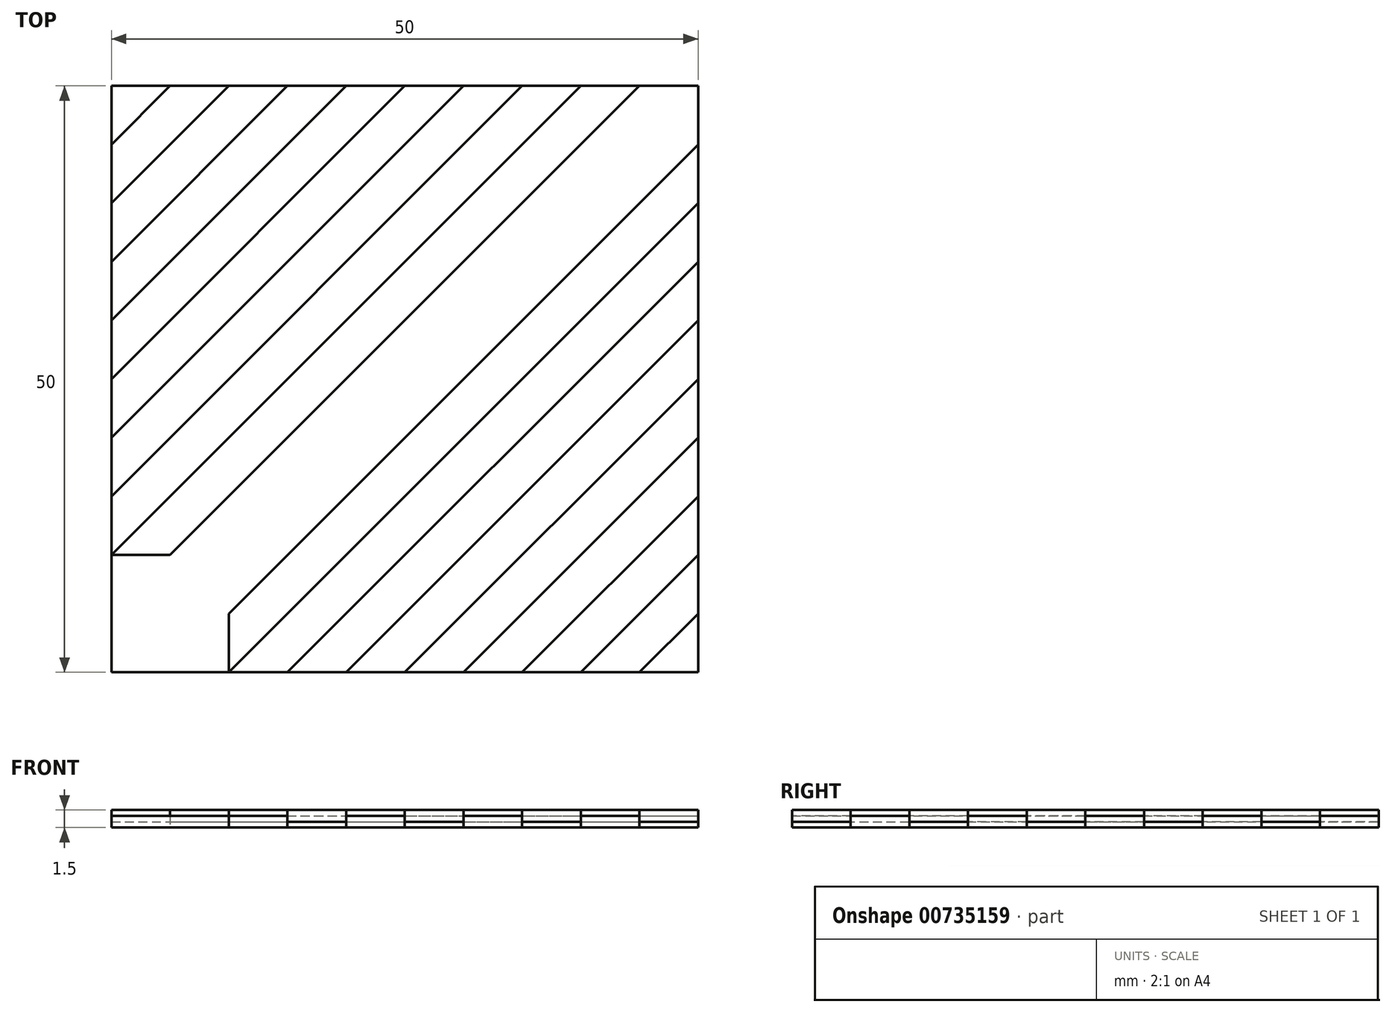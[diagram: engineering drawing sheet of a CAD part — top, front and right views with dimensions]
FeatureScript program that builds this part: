
annotation { "Feature Type Name" : "Feature", "Feature Type Description" : "" }
export const myFeature = defineFeature(function(context is Context, id is Id, definition is map)
    precondition{}
    {
        {
            var Q0;
            Q0=qCreatedBy(makeId("Top.planeOp"),FACE);
            var sketch = newSketch(context, id + "F0", { "sketchPlane" : qUnion([Q0])});
            skLineSegment(sketch, "E0.bottom", {"start": v(0, 50) * mm, "end": v(50, 50) * mm});
            skLineSegment(sketch, "E0.top", {"start": v(0, -50) * mm, "end": v(50, -50) * mm});
            skLineSegment(sketch, "E0.left", {"start": v(0, 50) * mm, "end": v(0, -50) * mm});
            skLineSegment(sketch, "E0.right", {"start": v(50, 50) * mm, "end": v(50, -50) * mm});
            skLineSegment(sketch, "E1", {"start": v(0, 10) * mm, "end": v(10, 10) * mm});
            skLineSegment(sketch, "E2", {"start": v(10, 10) * mm, "end": v(10, -10) * mm});
            skLineSegment(sketch, "E3", {"start": v(10, -10) * mm, "end": v(0, -10) * mm});
            skLineSegment(sketch, "E4", {"start": v(5, 10) * mm, "end": v(45, 50) * mm});
            skLineSegment(sketch, "E5", {"start": v(10, 10) * mm, "end": v(50, 50) * mm});
            skLineSegment(sketch, "E6", {"start": v(0, 10) * mm, "end": v(40, 50) * mm});
            skLineSegment(sketch, "E7", {"start": v(0, 15) * mm, "end": v(35, 50) * mm});
            skLineSegment(sketch, "E8", {"start": v(0, 20) * mm, "end": v(30, 50) * mm});
            skLineSegment(sketch, "E9", {"start": v(0, 25) * mm, "end": v(25, 50) * mm});
            skLineSegment(sketch, "E10", {"start": v(0, 30) * mm, "end": v(20, 50) * mm});
            skLineSegment(sketch, "E11", {"start": v(0, 35) * mm, "end": v(15, 50) * mm});
            skLineSegment(sketch, "E12", {"start": v(0, 40) * mm, "end": v(10, 50) * mm});
            skLineSegment(sketch, "E13", {"start": v(0, 45) * mm, "end": v(5, 50) * mm});
            skLineSegment(sketch, "E14", {"start": v(10, 5) * mm, "end": v(50, 45) * mm});
            skLineSegment(sketch, "E15", {"start": v(10, 0) * mm, "end": v(50, 40) * mm});
            skLineSegment(sketch, "E16", {"start": v(15, 0) * mm, "end": v(50, 35) * mm});
            skLineSegment(sketch, "E17", {"start": v(20, 0) * mm, "end": v(50, 30) * mm});
            skLineSegment(sketch, "E18", {"start": v(25, 0) * mm, "end": v(50, 25) * mm});
            skLineSegment(sketch, "E19", {"start": v(30, 0) * mm, "end": v(50, 20) * mm});
            skLineSegment(sketch, "E20", {"start": v(35, 0) * mm, "end": v(50, 15) * mm});
            skLineSegment(sketch, "E21", {"start": v(40, 0) * mm, "end": v(50, 10) * mm});
            skLineSegment(sketch, "E22", {"start": v(45, 0) * mm, "end": v(50, 5) * mm});
            skLineSegment(sketch, "E23", {"start": v(0, 0) * mm, "end": v(10, 0) * mm});
            skLineSegment(sketch, "E24", {"start": v(10, 0) * mm, "end": v(50, 0) * mm});
            skSolve(sketch);
        }
        {
            var Q0;
            {var subQ7=sQuery(id+"F0.wireOp",EDGE,"E23");Q0=makeQuery(id+"F0.imprint","IMPRINT",FACE,{"disambiguationData":[TD([[makeQuery(id+"F0.imprint","IMPRINT",EDGE,{"derivedFrom":subQ7}),1.0]])]});}
            var Q1;
            {var subQ2=sQuery(id+"F0.wireOp",EDGE,"E4");Q1=makeQuery(id+"F0.imprint","IMPRINT",FACE,{"disambiguationData":[TD([[makeQuery(id+"F0.imprint","IMPRINT",EDGE,{"derivedFrom":subQ2}),-1.0]])]});}
            var Q2;
            {var subQ0=sQuery(id+"F0.wireOp",EDGE,"E5");Q2=makeQuery(id+"F0.imprint","IMPRINT",FACE,{"disambiguationData":[TD([[makeQuery(id+"F0.imprint","IMPRINT",EDGE,{"derivedFrom":subQ0}),-1.0]])]});}
            var Q3;
            {var subQ0=sQuery(id+"F0.wireOp",EDGE,"E15");Q3=makeQuery(id+"F0.imprint","IMPRINT",FACE,{"disambiguationData":[TD([[makeQuery(id+"F0.imprint","IMPRINT",EDGE,{"derivedFrom":subQ0}),-1.0]])]});}
            var Q4;
            {var subQ0=sQuery(id+"F0.wireOp",EDGE,"E6");Q4=makeQuery(id+"F0.imprint","IMPRINT",FACE,{"disambiguationData":[TD([[makeQuery(id+"F0.imprint","IMPRINT",EDGE,{"derivedFrom":subQ0}),1.0]])]});}
            var Q5;
            {var subQ0=sQuery(id+"F0.wireOp",EDGE,"E17");Q5=makeQuery(id+"F0.imprint","IMPRINT",FACE,{"disambiguationData":[TD([[makeQuery(id+"F0.imprint","IMPRINT",EDGE,{"derivedFrom":subQ0}),-1.0]])]});}
            var Q6;
            {var subQ0=sQuery(id+"F0.wireOp",EDGE,"E8");Q6=makeQuery(id+"F0.imprint","IMPRINT",FACE,{"disambiguationData":[TD([[makeQuery(id+"F0.imprint","IMPRINT",EDGE,{"derivedFrom":subQ0}),1.0]])]});}
            var Q7;
            {var subQ0=sQuery(id+"F0.wireOp",EDGE,"E19");Q7=makeQuery(id+"F0.imprint","IMPRINT",FACE,{"disambiguationData":[TD([[makeQuery(id+"F0.imprint","IMPRINT",EDGE,{"derivedFrom":subQ0}),-1.0]])]});}
            var Q8;
            {var subQ0=sQuery(id+"F0.wireOp",EDGE,"E10");Q8=makeQuery(id+"F0.imprint","IMPRINT",FACE,{"disambiguationData":[TD([[makeQuery(id+"F0.imprint","IMPRINT",EDGE,{"derivedFrom":subQ0}),1.0]])]});}
            var Q9;
            {var subQ0=sQuery(id+"F0.wireOp",EDGE,"E21");Q9=makeQuery(id+"F0.imprint","IMPRINT",FACE,{"disambiguationData":[TD([[makeQuery(id+"F0.imprint","IMPRINT",EDGE,{"derivedFrom":subQ0}),-1.0]])]});}
            var Q10;
            {var subQ0=sQuery(id+"F0.wireOp",EDGE,"E12");Q10=makeQuery(id+"F0.imprint","IMPRINT",FACE,{"disambiguationData":[TD([[makeQuery(id+"F0.imprint","IMPRINT",EDGE,{"derivedFrom":subQ0}),1.0]])]});}
            extrude(context, id + "F1", {"entities" : qUnion([Q0, Q1, Q2, Q3, Q4, Q5, Q6, Q7, Q8, Q9, Q10]), "endBound" : BoundingType.SYMMETRIC, "depth" : 1 * mm, "offsetDistance" : 25 * mm});
        }
        {
            var Q0;
            {var subQ3=sQuery(id+"F0.wireOp",EDGE,"E13");Q0=makeQuery(id+"F0.imprint","IMPRINT",FACE,{"disambiguationData":[TD([[makeQuery(id+"F0.imprint","IMPRINT",EDGE,{"derivedFrom":subQ3}),1.0]])]});}
            var Q1;
            {var subQ0=sQuery(id+"F0.wireOp",EDGE,"E11");Q1=makeQuery(id+"F0.imprint","IMPRINT",FACE,{"disambiguationData":[TD([[makeQuery(id+"F0.imprint","IMPRINT",EDGE,{"derivedFrom":subQ0}),1.0]])]});}
            var Q2;
            {var subQ0=sQuery(id+"F0.wireOp",EDGE,"E9");Q2=makeQuery(id+"F0.imprint","IMPRINT",FACE,{"disambiguationData":[TD([[makeQuery(id+"F0.imprint","IMPRINT",EDGE,{"derivedFrom":subQ0}),1.0]])]});}
            var Q3;
            {var subQ0=sQuery(id+"F0.wireOp",EDGE,"E7");Q3=makeQuery(id+"F0.imprint","IMPRINT",FACE,{"disambiguationData":[TD([[makeQuery(id+"F0.imprint","IMPRINT",EDGE,{"derivedFrom":subQ0}),1.0]])]});}
            var Q4;
            {var subQ0=sQuery(id+"F0.wireOp",EDGE,"E4");Q4=makeQuery(id+"F0.imprint","IMPRINT",FACE,{"disambiguationData":[TD([[makeQuery(id+"F0.imprint","IMPRINT",EDGE,{"derivedFrom":subQ0}),1.0]])]});}
            var Q5;
            {var subQ0=sQuery(id+"F0.wireOp",EDGE,"E14");Q5=makeQuery(id+"F0.imprint","IMPRINT",FACE,{"disambiguationData":[TD([[makeQuery(id+"F0.imprint","IMPRINT",EDGE,{"derivedFrom":subQ0}),-1.0]])]});}
            var Q6;
            {var subQ0=sQuery(id+"F0.wireOp",EDGE,"E16");Q6=makeQuery(id+"F0.imprint","IMPRINT",FACE,{"disambiguationData":[TD([[makeQuery(id+"F0.imprint","IMPRINT",EDGE,{"derivedFrom":subQ0}),-1.0]])]});}
            var Q7;
            {var subQ0=sQuery(id+"F0.wireOp",EDGE,"E18");Q7=makeQuery(id+"F0.imprint","IMPRINT",FACE,{"disambiguationData":[TD([[makeQuery(id+"F0.imprint","IMPRINT",EDGE,{"derivedFrom":subQ0}),-1.0]])]});}
            var Q8;
            {var subQ0=sQuery(id+"F0.wireOp",EDGE,"E20");Q8=makeQuery(id+"F0.imprint","IMPRINT",FACE,{"disambiguationData":[TD([[makeQuery(id+"F0.imprint","IMPRINT",EDGE,{"derivedFrom":subQ0}),-1.0]])]});}
            var Q9;
            {var subQ0=sQuery(id+"F0.wireOp",EDGE,"E22");Q9=makeQuery(id+"F0.imprint","IMPRINT",FACE,{"disambiguationData":[TD([[makeQuery(id+"F0.imprint","IMPRINT",EDGE,{"derivedFrom":subQ0}),-1.0]])]});}
            extrude(context, id + "F2", {"entities" : qUnion([Q0, Q1, Q2, Q3, Q4, Q5, Q6, Q7, Q8, Q9]), "depth" : 1 * mm, "offsetDistance" : 25 * mm});
        }
    });
